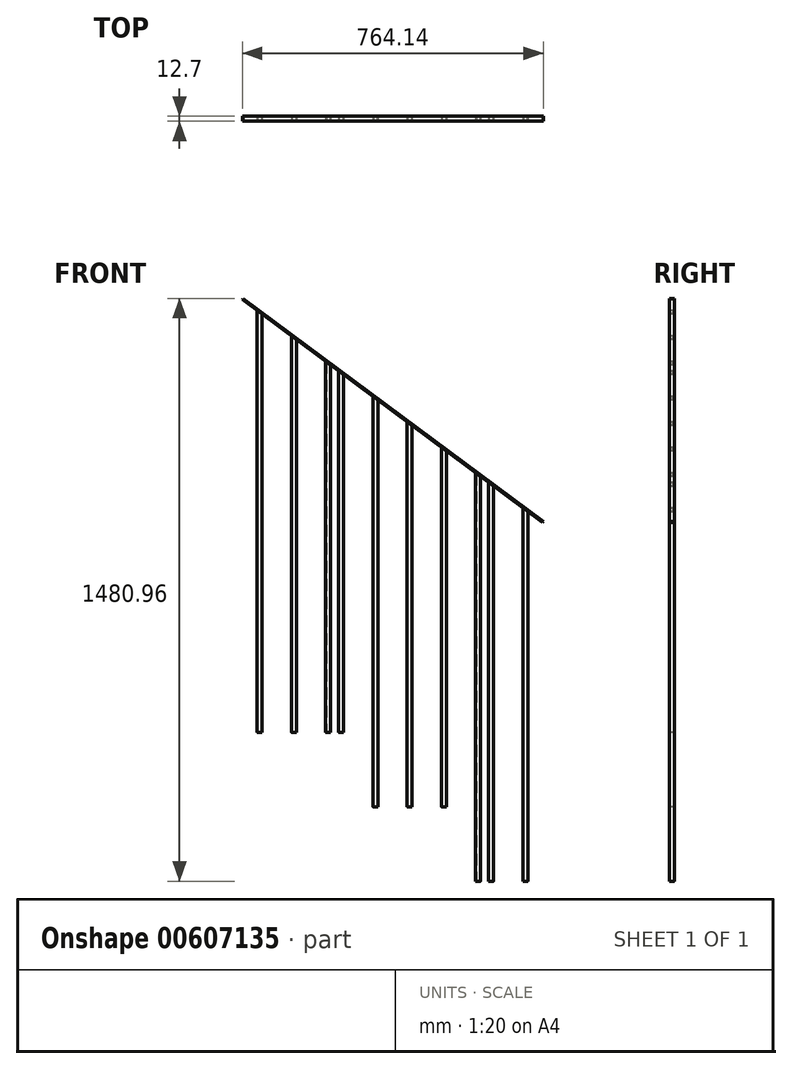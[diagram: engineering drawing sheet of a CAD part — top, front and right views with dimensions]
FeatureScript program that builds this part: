
annotation { "Feature Type Name" : "Feature", "Feature Type Description" : "" }
export const myFeature = defineFeature(function(context is Context, id is Id, definition is map)
    precondition{}
    {
        {
            var Q0;
            Q0=qCreatedBy(makeId("Top.planeOp"),FACE);
            var sketch = newSketch(context, id + "F0", { "sketchPlane" : qUnion([Q0])});
            skLineSegment(sketch, "E0.bottom", {"start": v(27.94, -6.35) * mm, "end": v(35.56, -6.35) * mm});
            skLineSegment(sketch, "E0.top", {"start": v(27.94, 6.35) * mm, "end": v(35.56, 6.35) * mm});
            skLineSegment(sketch, "E0.left", {"start": v(25.4, -3.81) * mm, "end": v(25.4, 3.8) * mm});
            skLineSegment(sketch, "E0.right", {"start": v(38.1, -3.8) * mm, "end": v(38.1, 3.81) * mm});
            skPoint(sketch, "E1.visualSharp", {"position": v(25.4, 6.35) * mm});
            skArc(sketch, "E1.filletArc", {"start": v(27.94, 6.35) * mm, "mid": v(26.14, 5.6) * mm, "end": v(25.4, 3.8) * mm});
            skPoint(sketch, "E2.visualSharp", {"position": v(25.4, -6.35) * mm});
            skArc(sketch, "E2.filletArc", {"start": v(25.4, -3.81) * mm, "mid": v(26.14, -5.6) * mm, "end": v(27.94, -6.35) * mm});
            skPoint(sketch, "E3.visualSharp", {"position": v(38.1, -6.35) * mm});
            skArc(sketch, "E3.filletArc", {"start": v(35.56, -6.35) * mm, "mid": v(37.36, -5.6) * mm, "end": v(38.1, -3.8) * mm});
            skPoint(sketch, "E4.visualSharp", {"position": v(38.1, 6.35) * mm});
            skArc(sketch, "E4.filletArc", {"start": v(38.1, 3.81) * mm, "mid": v(37.36, 5.6) * mm, "end": v(35.56, 6.35) * mm});
            skArc(sketch, "E5.0", {"start": v(27.94, 4.76) * mm, "mid": v(27.27, 4.48) * mm, "end": v(26.99, 3.81) * mm});
            skLineSegment(sketch, "E5.1", {"start": v(26.99, -3.81) * mm, "end": v(26.99, 3.81) * mm});
            skLineSegment(sketch, "E5.2", {"start": v(27.94, 4.76) * mm, "end": v(35.56, 4.76) * mm});
            skArc(sketch, "E5.3", {"start": v(26.99, -3.81) * mm, "mid": v(27.27, -4.48) * mm, "end": v(27.94, -4.76) * mm});
            skArc(sketch, "E5.4", {"start": v(36.51, 3.81) * mm, "mid": v(36.23, 4.48) * mm, "end": v(35.56, 4.76) * mm});
            skLineSegment(sketch, "E5.5", {"start": v(36.51, -3.81) * mm, "end": v(36.51, 3.81) * mm});
            skArc(sketch, "E5.6", {"start": v(35.56, -4.76) * mm, "mid": v(36.23, -4.48) * mm, "end": v(36.51, -3.81) * mm});
            skLineSegment(sketch, "E5.7", {"start": v(27.94, -4.76) * mm, "end": v(35.56, -4.76) * mm});
            skLineSegment(sketch, "E6.1.0.0", {"start": v(114.08, -3.81) * mm, "end": v(114.08, 3.81) * mm});
            skPoint(sketch, "E6.1.0.1", {"position": v(125.2, 6.35) * mm});
            skLineSegment(sketch, "E6.1.0.2", {"start": v(125.2, -3.8) * mm, "end": v(125.2, 3.81) * mm});
            skArc(sketch, "E6.1.0.3", {"start": v(125.2, 3.81) * mm, "mid": v(124.45, 5.6) * mm, "end": v(122.66, 6.35) * mm});
            skLineSegment(sketch, "E6.1.0.4", {"start": v(115.04, 6.35) * mm, "end": v(122.66, 6.35) * mm});
            skLineSegment(sketch, "E6.1.0.5", {"start": v(115.04, -6.35) * mm, "end": v(122.66, -6.35) * mm});
            skLineSegment(sketch, "E6.1.0.6", {"start": v(115.04, -4.76) * mm, "end": v(122.66, -4.76) * mm});
            skLineSegment(sketch, "E6.1.0.7", {"start": v(112.5, -3.81) * mm, "end": v(112.5, 3.8) * mm});
            skPoint(sketch, "E6.1.0.8", {"position": v(112.5, 6.35) * mm});
            skLineSegment(sketch, "E6.1.0.9", {"start": v(123.6, -3.81) * mm, "end": v(123.6, 3.81) * mm});
            skArc(sketch, "E6.1.0.10", {"start": v(122.66, -6.35) * mm, "mid": v(124.45, -5.6) * mm, "end": v(125.2, -3.8) * mm});
            skPoint(sketch, "E6.1.0.11", {"position": v(125.2, -6.35) * mm});
            skArc(sketch, "E6.1.0.12", {"start": v(115.04, 6.35) * mm, "mid": v(113.24, 5.6) * mm, "end": v(112.5, 3.8) * mm});
            skArc(sketch, "E6.1.0.13", {"start": v(112.5, -3.81) * mm, "mid": v(113.24, -5.6) * mm, "end": v(115.04, -6.35) * mm});
            skPoint(sketch, "E6.1.0.14", {"position": v(112.5, -6.35) * mm});
            skLineSegment(sketch, "E6.1.0.15", {"start": v(115.04, 4.76) * mm, "end": v(122.66, 4.76) * mm});
            skArc(sketch, "E6.1.0.16", {"start": v(115.04, 4.76) * mm, "mid": v(114.36, 4.48) * mm, "end": v(114.08, 3.81) * mm});
            skArc(sketch, "E6.1.0.17", {"start": v(122.66, -4.76) * mm, "mid": v(123.33, -4.48) * mm, "end": v(123.6, -3.81) * mm});
            skArc(sketch, "E6.1.0.18", {"start": v(114.08, -3.81) * mm, "mid": v(114.36, -4.48) * mm, "end": v(115.04, -4.76) * mm});
            skArc(sketch, "E6.1.0.19", {"start": v(123.6, 3.81) * mm, "mid": v(123.33, 4.48) * mm, "end": v(122.66, 4.76) * mm});
            skLineSegment(sketch, "E6.2.0.0", {"start": v(201.18, -3.81) * mm, "end": v(201.18, 3.81) * mm});
            skPoint(sketch, "E6.2.0.1", {"position": v(212.3, 6.35) * mm});
            skLineSegment(sketch, "E6.2.0.2", {"start": v(212.3, -3.8) * mm, "end": v(212.3, 3.81) * mm});
            skArc(sketch, "E6.2.0.3", {"start": v(212.3, 3.81) * mm, "mid": v(211.55, 5.6) * mm, "end": v(209.75, 6.35) * mm});
            skLineSegment(sketch, "E6.2.0.4", {"start": v(202.13, 6.35) * mm, "end": v(209.75, 6.35) * mm});
            skLineSegment(sketch, "E6.2.0.5", {"start": v(202.13, -6.35) * mm, "end": v(209.75, -6.35) * mm});
            skLineSegment(sketch, "E6.2.0.6", {"start": v(202.13, -4.76) * mm, "end": v(209.75, -4.76) * mm});
            skLineSegment(sketch, "E6.2.0.7", {"start": v(199.6, -3.81) * mm, "end": v(199.6, 3.8) * mm});
            skPoint(sketch, "E6.2.0.8", {"position": v(199.6, 6.35) * mm});
            skLineSegment(sketch, "E6.2.0.9", {"start": v(210.7, -3.81) * mm, "end": v(210.7, 3.81) * mm});
            skArc(sketch, "E6.2.0.10", {"start": v(209.75, -6.35) * mm, "mid": v(211.55, -5.6) * mm, "end": v(212.3, -3.8) * mm});
            skPoint(sketch, "E6.2.0.11", {"position": v(212.3, -6.35) * mm});
            skArc(sketch, "E6.2.0.12", {"start": v(202.13, 6.35) * mm, "mid": v(200.34, 5.6) * mm, "end": v(199.6, 3.8) * mm});
            skArc(sketch, "E6.2.0.13", {"start": v(199.6, -3.81) * mm, "mid": v(200.34, -5.6) * mm, "end": v(202.13, -6.35) * mm});
            skPoint(sketch, "E6.2.0.14", {"position": v(199.6, -6.35) * mm});
            skLineSegment(sketch, "E6.2.0.15", {"start": v(202.13, 4.76) * mm, "end": v(209.75, 4.76) * mm});
            skArc(sketch, "E6.2.0.16", {"start": v(202.13, 4.76) * mm, "mid": v(201.46, 4.48) * mm, "end": v(201.18, 3.81) * mm});
            skArc(sketch, "E6.2.0.17", {"start": v(209.75, -4.76) * mm, "mid": v(210.43, -4.48) * mm, "end": v(210.7, -3.81) * mm});
            skArc(sketch, "E6.2.0.18", {"start": v(201.18, -3.81) * mm, "mid": v(201.46, -4.48) * mm, "end": v(202.13, -4.76) * mm});
            skArc(sketch, "E6.2.0.19", {"start": v(210.7, 3.81) * mm, "mid": v(210.43, 4.48) * mm, "end": v(209.75, 4.76) * mm});
            skLineSegment(sketch, "E6.3.0.0", {"start": v(288.28, -3.81) * mm, "end": v(288.28, 3.81) * mm});
            skPoint(sketch, "E6.3.0.1", {"position": v(299.39, 6.35) * mm});
            skLineSegment(sketch, "E6.3.0.2", {"start": v(299.39, -3.8) * mm, "end": v(299.39, 3.81) * mm});
            skArc(sketch, "E6.3.0.3", {"start": v(299.39, 3.81) * mm, "mid": v(298.65, 5.6) * mm, "end": v(296.85, 6.35) * mm});
            skLineSegment(sketch, "E6.3.0.4", {"start": v(289.23, 6.35) * mm, "end": v(296.85, 6.35) * mm});
            skLineSegment(sketch, "E6.3.0.5", {"start": v(289.23, -6.35) * mm, "end": v(296.85, -6.35) * mm});
            skLineSegment(sketch, "E6.3.0.6", {"start": v(289.23, -4.76) * mm, "end": v(296.85, -4.76) * mm});
            skLineSegment(sketch, "E6.3.0.7", {"start": v(286.69, -3.81) * mm, "end": v(286.69, 3.8) * mm});
            skPoint(sketch, "E6.3.0.8", {"position": v(286.69, 6.35) * mm});
            skLineSegment(sketch, "E6.3.0.9", {"start": v(297.8, -3.81) * mm, "end": v(297.8, 3.81) * mm});
            skArc(sketch, "E6.3.0.10", {"start": v(296.85, -6.35) * mm, "mid": v(298.65, -5.6) * mm, "end": v(299.39, -3.8) * mm});
            skPoint(sketch, "E6.3.0.11", {"position": v(299.39, -6.35) * mm});
            skArc(sketch, "E6.3.0.12", {"start": v(289.23, 6.35) * mm, "mid": v(287.43, 5.6) * mm, "end": v(286.69, 3.8) * mm});
            skArc(sketch, "E6.3.0.13", {"start": v(286.69, -3.81) * mm, "mid": v(287.43, -5.6) * mm, "end": v(289.23, -6.35) * mm});
            skPoint(sketch, "E6.3.0.14", {"position": v(286.69, -6.35) * mm});
            skLineSegment(sketch, "E6.3.0.15", {"start": v(289.23, 4.76) * mm, "end": v(296.85, 4.76) * mm});
            skArc(sketch, "E6.3.0.16", {"start": v(289.23, 4.76) * mm, "mid": v(288.56, 4.48) * mm, "end": v(288.28, 3.81) * mm});
            skArc(sketch, "E6.3.0.17", {"start": v(296.85, -4.76) * mm, "mid": v(297.52, -4.48) * mm, "end": v(297.8, -3.81) * mm});
            skArc(sketch, "E6.3.0.18", {"start": v(288.28, -3.81) * mm, "mid": v(288.56, -4.48) * mm, "end": v(289.23, -4.76) * mm});
            skArc(sketch, "E6.3.0.19", {"start": v(297.8, 3.81) * mm, "mid": v(297.52, 4.48) * mm, "end": v(296.85, 4.76) * mm});
            skLineSegment(sketch, "E6.direction1", {"start": v(25.4, -6.35) * mm, "end": v(112.5, -6.35) * mm, "construction": true});
            skLineSegment(sketch, "E7.1.0.0", {"start": v(320.94, -3.81) * mm, "end": v(320.94, 3.81) * mm});
            skLineSegment(sketch, "E7.1.0.1", {"start": v(319.35, -3.81) * mm, "end": v(319.35, 3.8) * mm});
            skPoint(sketch, "E7.1.0.2", {"position": v(319.35, 6.35) * mm});
            skLineSegment(sketch, "E7.1.0.3", {"start": v(321.9, -6.35) * mm, "end": v(329.51, -6.35) * mm});
            skLineSegment(sketch, "E7.1.0.4", {"start": v(321.9, 4.76) * mm, "end": v(329.51, 4.76) * mm});
            skLineSegment(sketch, "E7.1.0.5", {"start": v(330.47, -3.81) * mm, "end": v(330.47, 3.81) * mm});
            skLineSegment(sketch, "E7.1.0.6", {"start": v(332.05, -3.8) * mm, "end": v(332.05, 3.81) * mm});
            skLineSegment(sketch, "E7.1.0.7", {"start": v(321.9, -4.76) * mm, "end": v(329.51, -4.76) * mm});
            skPoint(sketch, "E7.1.0.8", {"position": v(332.05, -6.35) * mm});
            skPoint(sketch, "E7.1.0.9", {"position": v(319.35, -6.35) * mm});
            skPoint(sketch, "E7.1.0.10", {"position": v(332.05, 6.35) * mm});
            skLineSegment(sketch, "E7.1.0.11", {"start": v(321.9, 6.35) * mm, "end": v(329.51, 6.35) * mm});
            skArc(sketch, "E7.1.0.12", {"start": v(320.94, -3.81) * mm, "mid": v(321.22, -4.48) * mm, "end": v(321.9, -4.76) * mm});
            skArc(sketch, "E7.1.0.13", {"start": v(319.35, -3.81) * mm, "mid": v(320.1, -5.6) * mm, "end": v(321.9, -6.35) * mm});
            skArc(sketch, "E7.1.0.14", {"start": v(329.51, -6.35) * mm, "mid": v(331.31, -5.6) * mm, "end": v(332.05, -3.8) * mm});
            skArc(sketch, "E7.1.0.15", {"start": v(321.9, 4.76) * mm, "mid": v(321.22, 4.48) * mm, "end": v(320.94, 3.81) * mm});
            skArc(sketch, "E7.1.0.16", {"start": v(330.47, 3.81) * mm, "mid": v(330.19, 4.48) * mm, "end": v(329.51, 4.76) * mm});
            skArc(sketch, "E7.1.0.17", {"start": v(321.9, 6.35) * mm, "mid": v(320.1, 5.6) * mm, "end": v(319.35, 3.8) * mm});
            skArc(sketch, "E7.1.0.18", {"start": v(332.05, 3.81) * mm, "mid": v(331.31, 5.6) * mm, "end": v(329.51, 6.35) * mm});
            skArc(sketch, "E7.1.0.19", {"start": v(329.51, -4.76) * mm, "mid": v(330.19, -4.48) * mm, "end": v(330.47, -3.81) * mm});
            skLineSegment(sketch, "E7.direction1", {"start": v(286.69, -6.35) * mm, "end": v(319.35, -6.35) * mm, "construction": true});
            skPoint(sketch, "E8.1.0.0", {"position": v(580.6, -6.35) * mm});
            skPoint(sketch, "E8.1.0.1", {"position": v(667.69, 6.35) * mm});
            skPoint(sketch, "E8.1.0.2", {"position": v(406.4, 6.35) * mm});
            skPoint(sketch, "E8.1.0.3", {"position": v(406.4, -6.35) * mm});
            skPoint(sketch, "E8.1.0.4", {"position": v(680.39, -6.35) * mm});
            skLineSegment(sketch, "E8.1.0.5", {"start": v(406.4, -6.35) * mm, "end": v(493.5, -6.35) * mm, "construction": true});
            skPoint(sketch, "E8.1.0.6", {"position": v(680.39, 6.35) * mm});
            skPoint(sketch, "E8.1.0.7", {"position": v(506.2, -6.35) * mm});
            skPoint(sketch, "E8.1.0.8", {"position": v(419.1, -6.35) * mm});
            skPoint(sketch, "E8.1.0.9", {"position": v(667.69, -6.35) * mm});
            skPoint(sketch, "E8.1.0.10", {"position": v(506.2, 6.35) * mm});
            skPoint(sketch, "E8.1.0.11", {"position": v(593.3, 6.35) * mm});
            skPoint(sketch, "E8.1.0.12", {"position": v(593.3, -6.35) * mm});
            skPoint(sketch, "E8.1.0.13", {"position": v(419.1, 6.35) * mm});
            skPoint(sketch, "E8.1.0.14", {"position": v(713.05, -6.35) * mm});
            skPoint(sketch, "E8.1.0.15", {"position": v(700.35, 6.35) * mm});
            skPoint(sketch, "E8.1.0.16", {"position": v(713.05, 6.35) * mm});
            skPoint(sketch, "E8.1.0.17", {"position": v(493.5, -6.35) * mm});
            skPoint(sketch, "E8.1.0.18", {"position": v(580.6, 6.35) * mm});
            skPoint(sketch, "E8.1.0.19", {"position": v(493.5, 6.35) * mm});
            skPoint(sketch, "E8.1.0.20", {"position": v(700.35, -6.35) * mm});
            skLineSegment(sketch, "E8.1.0.21", {"start": v(408.94, -6.35) * mm, "end": v(416.56, -6.35) * mm});
            skLineSegment(sketch, "E8.1.0.22", {"start": v(419.1, -3.8) * mm, "end": v(419.1, 3.81) * mm});
            skArc(sketch, "E8.1.0.23", {"start": v(407.99, -3.81) * mm, "mid": v(408.27, -4.48) * mm, "end": v(408.94, -4.76) * mm});
            skArc(sketch, "E8.1.0.24", {"start": v(417.51, 3.81) * mm, "mid": v(417.23, 4.48) * mm, "end": v(416.56, 4.76) * mm});
            skLineSegment(sketch, "E8.1.0.25", {"start": v(408.94, 4.76) * mm, "end": v(416.56, 4.76) * mm});
            skLineSegment(sketch, "E8.1.0.26", {"start": v(670.23, 6.35) * mm, "end": v(677.85, 6.35) * mm});
            skArc(sketch, "E8.1.0.27", {"start": v(406.4, -3.81) * mm, "mid": v(407.14, -5.6) * mm, "end": v(408.94, -6.35) * mm});
            skArc(sketch, "E8.1.0.28", {"start": v(408.94, 6.35) * mm, "mid": v(407.14, 5.6) * mm, "end": v(406.4, 3.8) * mm});
            skLineSegment(sketch, "E8.1.0.29", {"start": v(407.99, -3.81) * mm, "end": v(407.99, 3.81) * mm});
            skArc(sketch, "E8.1.0.30", {"start": v(416.56, -6.35) * mm, "mid": v(418.36, -5.6) * mm, "end": v(419.1, -3.8) * mm});
            skLineSegment(sketch, "E8.1.0.31", {"start": v(408.94, 6.35) * mm, "end": v(416.56, 6.35) * mm});
            skArc(sketch, "E8.1.0.32", {"start": v(416.56, -4.76) * mm, "mid": v(417.23, -4.48) * mm, "end": v(417.51, -3.81) * mm});
            skLineSegment(sketch, "E8.1.0.33", {"start": v(406.4, -3.81) * mm, "end": v(406.4, 3.8) * mm});
            skLineSegment(sketch, "E8.1.0.34", {"start": v(408.94, -4.76) * mm, "end": v(416.56, -4.76) * mm});
            skLineSegment(sketch, "E8.1.0.35", {"start": v(417.51, -3.81) * mm, "end": v(417.51, 3.81) * mm});
            skArc(sketch, "E8.1.0.36", {"start": v(419.1, 3.81) * mm, "mid": v(418.36, 5.6) * mm, "end": v(416.56, 6.35) * mm});
            skArc(sketch, "E8.1.0.37", {"start": v(408.94, 4.76) * mm, "mid": v(408.27, 4.48) * mm, "end": v(407.99, 3.81) * mm});
            skLineSegment(sketch, "E8.1.0.38", {"start": v(496.04, -6.35) * mm, "end": v(503.66, -6.35) * mm});
            skLineSegment(sketch, "E8.1.0.39", {"start": v(580.6, -3.81) * mm, "end": v(580.6, 3.8) * mm});
            skArc(sketch, "E8.1.0.40", {"start": v(669.28, -3.81) * mm, "mid": v(669.56, -4.48) * mm, "end": v(670.23, -4.76) * mm});
            skArc(sketch, "E8.1.0.41", {"start": v(667.69, -3.81) * mm, "mid": v(668.43, -5.6) * mm, "end": v(670.23, -6.35) * mm});
            skArc(sketch, "E8.1.0.42", {"start": v(670.23, 4.76) * mm, "mid": v(669.56, 4.48) * mm, "end": v(669.28, 3.81) * mm});
            skLineSegment(sketch, "E8.1.0.43", {"start": v(670.23, 4.76) * mm, "end": v(677.85, 4.76) * mm});
            skLineSegment(sketch, "E8.1.0.44", {"start": v(667.69, -3.81) * mm, "end": v(667.69, 3.8) * mm});
            skArc(sketch, "E8.1.0.45", {"start": v(677.85, -6.35) * mm, "mid": v(679.65, -5.6) * mm, "end": v(680.39, -3.8) * mm});
            skArc(sketch, "E8.1.0.46", {"start": v(680.39, 3.81) * mm, "mid": v(679.65, 5.6) * mm, "end": v(677.85, 6.35) * mm});
            skArc(sketch, "E8.1.0.47", {"start": v(678.8, 3.81) * mm, "mid": v(678.52, 4.48) * mm, "end": v(677.85, 4.76) * mm});
            skLineSegment(sketch, "E8.1.0.48", {"start": v(506.2, -3.8) * mm, "end": v(506.2, 3.81) * mm});
            skLineSegment(sketch, "E8.1.0.49", {"start": v(680.39, -3.8) * mm, "end": v(680.39, 3.81) * mm});
            skLineSegment(sketch, "E8.1.0.50", {"start": v(667.69, -6.35) * mm, "end": v(700.35, -6.35) * mm, "construction": true});
            skArc(sketch, "E8.1.0.51", {"start": v(503.66, -6.35) * mm, "mid": v(505.45, -5.6) * mm, "end": v(506.2, -3.8) * mm});
            skArc(sketch, "E8.1.0.52", {"start": v(496.04, 4.76) * mm, "mid": v(495.36, 4.48) * mm, "end": v(495.08, 3.81) * mm});
            skLineSegment(sketch, "E8.1.0.53", {"start": v(496.04, -4.76) * mm, "end": v(503.66, -4.76) * mm});
            skArc(sketch, "E8.1.0.54", {"start": v(590.75, -6.35) * mm, "mid": v(592.55, -5.6) * mm, "end": v(593.3, -3.8) * mm});
            skArc(sketch, "E8.1.0.55", {"start": v(493.5, -3.81) * mm, "mid": v(494.24, -5.6) * mm, "end": v(496.04, -6.35) * mm});
            skLineSegment(sketch, "E8.1.0.56", {"start": v(583.13, 6.35) * mm, "end": v(590.75, 6.35) * mm});
            skArc(sketch, "E8.1.0.57", {"start": v(713.05, 3.81) * mm, "mid": v(712.31, 5.6) * mm, "end": v(710.51, 6.35) * mm});
            skLineSegment(sketch, "E8.1.0.58", {"start": v(496.04, 6.35) * mm, "end": v(503.66, 6.35) * mm});
            skArc(sketch, "E8.1.0.59", {"start": v(580.6, -3.81) * mm, "mid": v(581.34, -5.6) * mm, "end": v(583.13, -6.35) * mm});
            skArc(sketch, "E8.1.0.60", {"start": v(590.75, -4.76) * mm, "mid": v(591.43, -4.48) * mm, "end": v(591.7, -3.81) * mm});
            skLineSegment(sketch, "E8.1.0.61", {"start": v(669.28, -3.81) * mm, "end": v(669.28, 3.81) * mm});
            skLineSegment(sketch, "E8.1.0.62", {"start": v(493.5, -3.81) * mm, "end": v(493.5, 3.8) * mm});
            skArc(sketch, "E8.1.0.63", {"start": v(583.13, 4.76) * mm, "mid": v(582.46, 4.48) * mm, "end": v(582.18, 3.81) * mm});
            skArc(sketch, "E8.1.0.64", {"start": v(496.04, 6.35) * mm, "mid": v(494.24, 5.6) * mm, "end": v(493.5, 3.8) * mm});
            skArc(sketch, "E8.1.0.65", {"start": v(702.9, 6.35) * mm, "mid": v(701.1, 5.6) * mm, "end": v(700.35, 3.8) * mm});
            skLineSegment(sketch, "E8.1.0.66", {"start": v(701.94, -3.81) * mm, "end": v(701.94, 3.81) * mm});
            skLineSegment(sketch, "E8.1.0.67", {"start": v(582.18, -3.81) * mm, "end": v(582.18, 3.81) * mm});
            skLineSegment(sketch, "E8.1.0.68", {"start": v(711.47, -3.81) * mm, "end": v(711.47, 3.81) * mm});
            skLineSegment(sketch, "E8.1.0.69", {"start": v(702.9, -6.35) * mm, "end": v(710.51, -6.35) * mm});
            skArc(sketch, "E8.1.0.70", {"start": v(670.23, 6.35) * mm, "mid": v(668.43, 5.6) * mm, "end": v(667.69, 3.8) * mm});
            skArc(sketch, "E8.1.0.71", {"start": v(593.3, 3.81) * mm, "mid": v(592.55, 5.6) * mm, "end": v(590.75, 6.35) * mm});
            skLineSegment(sketch, "E8.1.0.72", {"start": v(670.23, -4.76) * mm, "end": v(677.85, -4.76) * mm});
            skArc(sketch, "E8.1.0.73", {"start": v(710.51, -6.35) * mm, "mid": v(712.31, -5.6) * mm, "end": v(713.05, -3.8) * mm});
            skLineSegment(sketch, "E8.1.0.74", {"start": v(504.6, -3.81) * mm, "end": v(504.6, 3.81) * mm});
            skLineSegment(sketch, "E8.1.0.75", {"start": v(593.3, -3.8) * mm, "end": v(593.3, 3.81) * mm});
            skLineSegment(sketch, "E8.1.0.76", {"start": v(670.23, -6.35) * mm, "end": v(677.85, -6.35) * mm});
            skLineSegment(sketch, "E8.1.0.77", {"start": v(700.35, -3.81) * mm, "end": v(700.35, 3.8) * mm});
            skArc(sketch, "E8.1.0.78", {"start": v(591.7, 3.81) * mm, "mid": v(591.43, 4.48) * mm, "end": v(590.75, 4.76) * mm});
            skLineSegment(sketch, "E8.1.0.79", {"start": v(702.9, 6.35) * mm, "end": v(710.51, 6.35) * mm});
            skArc(sketch, "E8.1.0.80", {"start": v(504.6, 3.81) * mm, "mid": v(504.33, 4.48) * mm, "end": v(503.66, 4.76) * mm});
            skLineSegment(sketch, "E8.1.0.81", {"start": v(713.05, -3.8) * mm, "end": v(713.05, 3.81) * mm});
            skLineSegment(sketch, "E8.1.0.82", {"start": v(678.8, -3.81) * mm, "end": v(678.8, 3.81) * mm});
            skLineSegment(sketch, "E8.1.0.83", {"start": v(583.13, -4.76) * mm, "end": v(590.75, -4.76) * mm});
            skLineSegment(sketch, "E8.1.0.84", {"start": v(583.13, -6.35) * mm, "end": v(590.75, -6.35) * mm});
            skArc(sketch, "E8.1.0.85", {"start": v(495.08, -3.81) * mm, "mid": v(495.36, -4.48) * mm, "end": v(496.04, -4.76) * mm});
            skArc(sketch, "E8.1.0.86", {"start": v(677.85, -4.76) * mm, "mid": v(678.52, -4.48) * mm, "end": v(678.8, -3.81) * mm});
            skLineSegment(sketch, "E8.1.0.87", {"start": v(591.7, -3.81) * mm, "end": v(591.7, 3.81) * mm});
            skArc(sketch, "E8.1.0.88", {"start": v(506.2, 3.81) * mm, "mid": v(505.45, 5.6) * mm, "end": v(503.66, 6.35) * mm});
            skArc(sketch, "E8.1.0.89", {"start": v(583.13, 6.35) * mm, "mid": v(581.34, 5.6) * mm, "end": v(580.6, 3.8) * mm});
            skLineSegment(sketch, "E8.1.0.90", {"start": v(496.04, 4.76) * mm, "end": v(503.66, 4.76) * mm});
            skArc(sketch, "E8.1.0.91", {"start": v(700.35, -3.81) * mm, "mid": v(701.1, -5.6) * mm, "end": v(702.9, -6.35) * mm});
            skArc(sketch, "E8.1.0.92", {"start": v(710.51, -4.76) * mm, "mid": v(711.19, -4.48) * mm, "end": v(711.47, -3.81) * mm});
            skLineSegment(sketch, "E8.1.0.93", {"start": v(702.9, 4.76) * mm, "end": v(710.51, 4.76) * mm});
            skArc(sketch, "E8.1.0.94", {"start": v(702.9, 4.76) * mm, "mid": v(702.22, 4.48) * mm, "end": v(701.94, 3.81) * mm});
            skLineSegment(sketch, "E8.1.0.95", {"start": v(702.9, -4.76) * mm, "end": v(710.51, -4.76) * mm});
            skArc(sketch, "E8.1.0.96", {"start": v(582.18, -3.81) * mm, "mid": v(582.46, -4.48) * mm, "end": v(583.13, -4.76) * mm});
            skLineSegment(sketch, "E8.1.0.97", {"start": v(583.13, 4.76) * mm, "end": v(590.75, 4.76) * mm});
            skArc(sketch, "E8.1.0.98", {"start": v(503.66, -4.76) * mm, "mid": v(504.33, -4.48) * mm, "end": v(504.6, -3.81) * mm});
            skArc(sketch, "E8.1.0.99", {"start": v(711.47, 3.81) * mm, "mid": v(711.19, 4.48) * mm, "end": v(710.51, 4.76) * mm});
            skLineSegment(sketch, "E8.1.0.100", {"start": v(495.08, -3.81) * mm, "end": v(495.08, 3.81) * mm});
            skArc(sketch, "E8.1.0.101", {"start": v(701.94, -3.81) * mm, "mid": v(702.22, -4.48) * mm, "end": v(702.9, -4.76) * mm});
            skLineSegment(sketch, "E8.direction1", {"start": v(25.4, -6.35) * mm, "end": v(406.4, -6.35) * mm, "construction": true});
            skLineSegment(sketch, "E9.1.0.0", {"start": v(798.56, -3.81) * mm, "end": v(798.56, 3.81) * mm});
            skLineSegment(sketch, "E9.1.0.1", {"start": v(800.15, -3.8) * mm, "end": v(800.15, 3.81) * mm});
            skLineSegment(sketch, "E9.1.0.2", {"start": v(790, -6.35) * mm, "end": v(797.61, -6.35) * mm});
            skPoint(sketch, "E9.1.0.3", {"position": v(787.45, 6.35) * mm});
            skLineSegment(sketch, "E9.1.0.4", {"start": v(789.04, -3.81) * mm, "end": v(789.04, 3.81) * mm});
            skPoint(sketch, "E9.1.0.5", {"position": v(800.15, 6.35) * mm});
            skLineSegment(sketch, "E9.1.0.6", {"start": v(790, 4.76) * mm, "end": v(797.61, 4.76) * mm});
            skLineSegment(sketch, "E9.1.0.7", {"start": v(787.45, -3.81) * mm, "end": v(787.45, 3.8) * mm});
            skLineSegment(sketch, "E9.1.0.8", {"start": v(790, -4.76) * mm, "end": v(797.61, -4.76) * mm});
            skLineSegment(sketch, "E9.1.0.9", {"start": v(790, 6.35) * mm, "end": v(797.61, 6.35) * mm});
            skPoint(sketch, "E9.1.0.10", {"position": v(787.45, -6.35) * mm});
            skPoint(sketch, "E9.1.0.11", {"position": v(800.15, -6.35) * mm});
            skArc(sketch, "E9.1.0.12", {"start": v(787.45, -3.81) * mm, "mid": v(788.2, -5.6) * mm, "end": v(790, -6.35) * mm});
            skArc(sketch, "E9.1.0.13", {"start": v(790, 6.35) * mm, "mid": v(788.2, 5.6) * mm, "end": v(787.45, 3.8) * mm});
            skArc(sketch, "E9.1.0.14", {"start": v(790, 4.76) * mm, "mid": v(789.32, 4.48) * mm, "end": v(789.04, 3.81) * mm});
            skArc(sketch, "E9.1.0.15", {"start": v(789.04, -3.81) * mm, "mid": v(789.32, -4.48) * mm, "end": v(790, -4.76) * mm});
            skArc(sketch, "E9.1.0.16", {"start": v(797.61, -6.35) * mm, "mid": v(799.4, -5.6) * mm, "end": v(800.15, -3.8) * mm});
            skArc(sketch, "E9.1.0.17", {"start": v(800.15, 3.81) * mm, "mid": v(799.4, 5.6) * mm, "end": v(797.61, 6.35) * mm});
            skArc(sketch, "E9.1.0.18", {"start": v(798.56, 3.81) * mm, "mid": v(798.28, 4.48) * mm, "end": v(797.61, 4.76) * mm});
            skArc(sketch, "E9.1.0.19", {"start": v(797.61, -4.76) * mm, "mid": v(798.28, -4.48) * mm, "end": v(798.56, -3.81) * mm});
            skLineSegment(sketch, "E9.direction1", {"start": v(700.35, -6.35) * mm, "end": v(787.45, -6.35) * mm, "construction": true});
            skSolve(sketch);
        }
        {
            var Q0;
            Q0 = qSketchRegion(id + "F0", true);
            extrude(context, id + "F1", {"entities" : qUnion([Q0]), "depth" : 1676.4 * mm, "offsetDistance" : 25.4 * mm});
        }
        {
            var Q0;
            Q0=qCreatedBy(makeId("Front.planeOp"),FACE);
            var sketch = newSketch(context, id + "F2", { "sketchPlane" : qUnion([Q0])});
            skLineSegment(sketch, "E10", {"start": v(841.32, 0) * mm, "end": v(605.1, 0) * mm});
            skLineSegment(sketch, "E11", {"start": v(605.1, 0) * mm, "end": v(605.1, 189.1) * mm});
            skLineSegment(sketch, "E12", {"start": v(605.1, 189.1) * mm, "end": v(351.1, 189.1) * mm});
            skLineSegment(sketch, "E13", {"start": v(351.1, 189.1) * mm, "end": v(351.1, 378.2) * mm});
            skLineSegment(sketch, "E14", {"start": v(351.1, 378.2) * mm, "end": v(97.1, 378.2) * mm});
            skLineSegment(sketch, "E15", {"start": v(97.1, 378.2) * mm, "end": v(97.1, 1778) * mm});
            skLineSegment(sketch, "E16", {"start": v(-146.46, -254) * mm, "end": v(1316.21, -254) * mm});
            skLineSegment(sketch, "E17", {"start": v(841.32, 0) * mm, "end": v(841.32, 908.05) * mm});
            skLineSegment(sketch, "E18", {"start": v(841.32, 908.05) * mm, "end": v(101.52, 1458.82) * mm});
            skLineSegment(sketch, "E19", {"start": v(1316.21, -254) * mm, "end": v(1316.21, 1778) * mm});
            skLineSegment(sketch, "E20", {"start": v(1316.21, 1778) * mm, "end": v(101.52, 1778) * mm});
            skLineSegment(sketch, "E21", {"start": v(101.52, 1458.82) * mm, "end": v(101.52, 1778) * mm});
            skLineSegment(sketch, "E22", {"start": v(-146.46, -254) * mm, "end": v(-146.46, 1778) * mm});
            skLineSegment(sketch, "E23", {"start": v(-146.46, 1778) * mm, "end": v(97.1, 1778) * mm});
            skSolve(sketch);
        }
        {
            var Q0;
            Q0 = qSketchRegion(id + "F2", true);
            extrude(context, id + "F3", {"entities" : qUnion([Q0]), "operationType" : NewBodyOperationType.REMOVE, "endBound" : BoundingType.SYMMETRIC, "depth" : 25.4 * mm, "offsetDistance" : 25.4 * mm});
        }
        {
            var Q0;
            Q0=qCreatedBy(makeId("Front.planeOp"),FACE);
            var sketch = newSketch(context, id + "F4", { "sketchPlane" : qUnion([Q0])});
            skLineSegment(sketch, "E24", {"start": v(75.2, 1478.41) * mm, "end": v(837.45, 910.94) * mm});
            skLineSegment(sketch, "E25.0", {"start": v(77.1, 1480.96) * mm, "end": v(839.34, 913.48) * mm});
            skLineSegment(sketch, "E26", {"start": v(75.2, 1478.41) * mm, "end": v(77.1, 1480.96) * mm});
            skLineSegment(sketch, "E27", {"start": v(837.45, 910.94) * mm, "end": v(839.34, 913.48) * mm});
            skSolve(sketch);
        }
        {
            var Q0;
            Q0 = qSketchRegion(id + "F4", true);
            extrude(context, id + "F5", {"entities" : qUnion([Q0]), "endBound" : BoundingType.SYMMETRIC, "depth" : 12.7 * mm, "offsetDistance" : 25.4 * mm});
        }
    });
